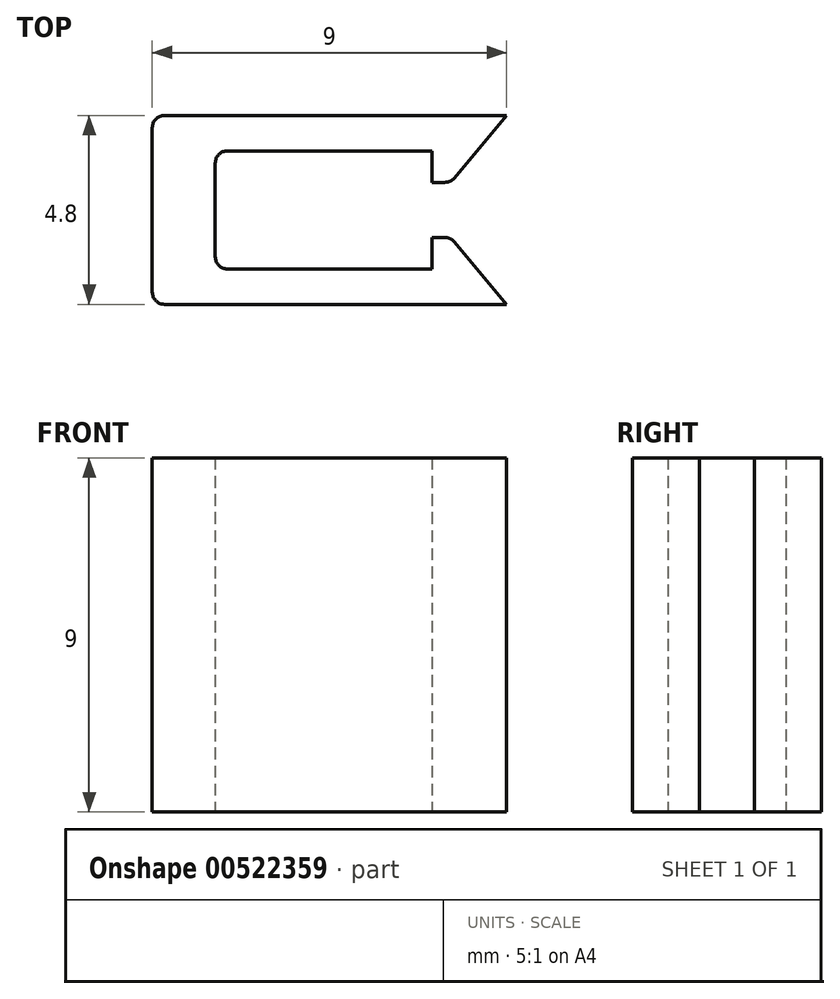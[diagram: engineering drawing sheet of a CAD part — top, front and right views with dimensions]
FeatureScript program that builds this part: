
annotation { "Feature Type Name" : "Feature", "Feature Type Description" : "" }
export const myFeature = defineFeature(function(context is Context, id is Id, definition is map)
    precondition{}
    {
        {
            var Q0;
            Q0=qCreatedBy(makeId("Top.planeOp"),FACE);
            var sketch = newSketch(context, id + "F0", { "sketchPlane" : qUnion([Q0])});
            skLineSegment(sketch, "E0.bottom", {"start": v(4.5, -2.4) * mm, "end": v(-4.19, -2.4) * mm});
            skLineSegment(sketch, "E0.top", {"start": v(4.5, 2.4) * mm, "end": v(-4.19, 2.4) * mm});
            skLineSegment(sketch, "E0.right", {"start": v(-4.5, -2.09) * mm, "end": v(-4.5, 2.09) * mm});
            skPoint(sketch, "E0.middle", {"position": v(0, 0) * mm});
            skLineSegment(sketch, "E1.bottom", {"start": v(2.6, 1.5) * mm, "end": v(-2.59, 1.5) * mm});
            skLineSegment(sketch, "E1.top", {"start": v(2.6, -1.5) * mm, "end": v(-2.59, -1.5) * mm});
            skLineSegment(sketch, "E1.right", {"start": v(-2.9, 1.19) * mm, "end": v(-2.9, -1.19) * mm});
            skLineSegment(sketch, "E2", {"start": v(4.5, 0) * mm, "end": v(-4.5, 0) * mm, "construction": true});
            skLineSegment(sketch, "E3.top", {"start": v(2.93, 0.7) * mm, "end": v(2.6, 0.7) * mm});
            skLineSegment(sketch, "E3.right", {"start": v(2.6, 1.5) * mm, "end": v(2.6, 0.7) * mm});
            skLineSegment(sketch, "E4", {"start": v(3.17, 0.81) * mm, "end": v(4.5, 2.4) * mm});
            skLineSegment(sketch, "E5", {"start": v(2.6, -1.5) * mm, "end": v(2.6, -0.7) * mm});
            skLineSegment(sketch, "E6", {"start": v(2.6, -0.7) * mm, "end": v(2.93, -0.7) * mm});
            skLineSegment(sketch, "E7", {"start": v(3.17, -0.81) * mm, "end": v(4.5, -2.4) * mm});
            skPoint(sketch, "E8.visualSharp", {"position": v(-4.5, 2.4) * mm});
            skArc(sketch, "E8.filletArc", {"start": v(-4.19, 2.4) * mm, "mid": v(-4.4, 2.3) * mm, "end": v(-4.5, 2.09) * mm});
            skPoint(sketch, "E9.visualSharp", {"position": v(-4.5, -2.4) * mm});
            skArc(sketch, "E9.filletArc", {"start": v(-4.5, -2.09) * mm, "mid": v(-4.4, -2.3) * mm, "end": v(-4.19, -2.4) * mm});
            skPoint(sketch, "E10.visualSharp", {"position": v(-2.9, 1.5) * mm});
            skArc(sketch, "E10.filletArc", {"start": v(-2.59, 1.5) * mm, "mid": v(-2.8, 1.4) * mm, "end": v(-2.9, 1.19) * mm});
            skPoint(sketch, "E11.visualSharp", {"position": v(-2.9, -1.5) * mm});
            skArc(sketch, "E11.filletArc", {"start": v(-2.9, -1.19) * mm, "mid": v(-2.8, -1.4) * mm, "end": v(-2.59, -1.5) * mm});
            skPoint(sketch, "E12.visualSharp", {"position": v(3.08, -0.7) * mm});
            skArc(sketch, "E12.filletArc", {"start": v(3.17, -0.81) * mm, "mid": v(3.07, -0.73) * mm, "end": v(2.93, -0.7) * mm});
            skPoint(sketch, "E13.visualSharp", {"position": v(3.08, 0.7) * mm});
            skArc(sketch, "E13.filletArc", {"start": v(2.93, 0.7) * mm, "mid": v(3.07, 0.73) * mm, "end": v(3.17, 0.81) * mm});
            skSolve(sketch);
        }
        {
            var Q0;
            Q0=makeQuery(id+"F0.imprint","IMPRINT",FACE,{"disambiguationData":[TD([[makeQuery(id+"F0.imprint","IMPRINT",EDGE,{"derivedFrom":sQuery(id+"F0.wireOp",EDGE,"E0.bottom")}),-1.0]])]});
            extrude(context, id + "F1", {"entities" : qUnion([Q0]), "depth" : 9 * mm, "offsetDistance" : 25 * mm});
        }
    });
